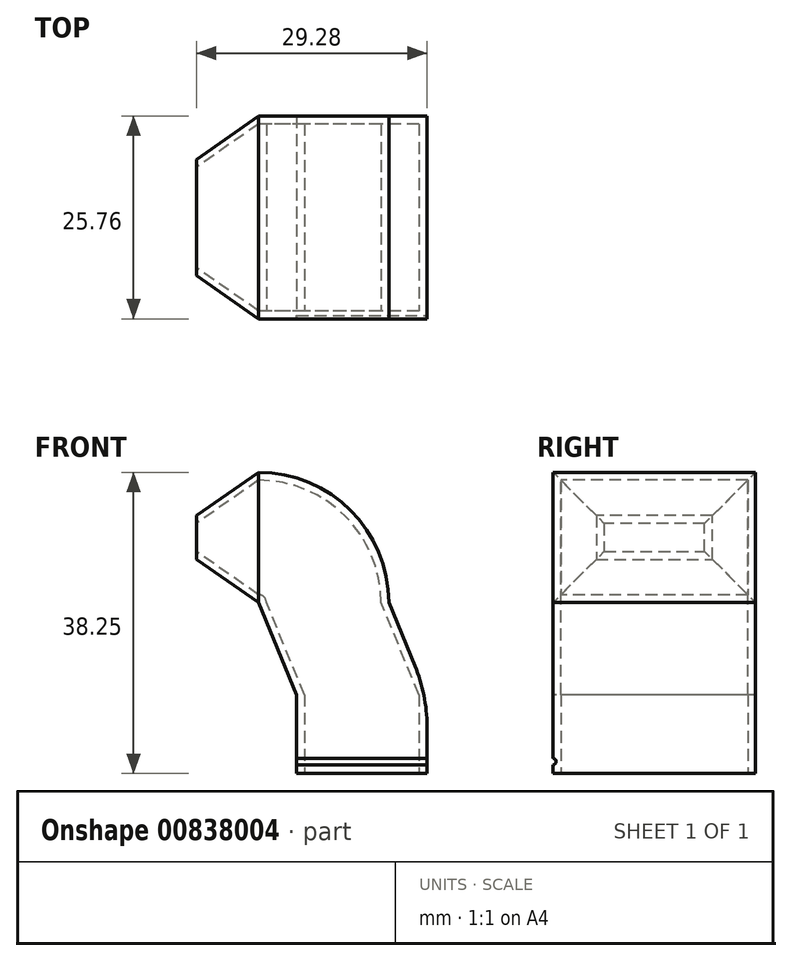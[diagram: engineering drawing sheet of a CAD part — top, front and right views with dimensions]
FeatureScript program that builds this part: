
annotation { "Feature Type Name" : "Feature", "Feature Type Description" : "" }
export const myFeature = defineFeature(function(context is Context, id is Id, definition is map)
    precondition{}
    {
        {
            var Q0;
            Q0=qCreatedBy(makeId("Top.planeOp"),FACE);
            var sketch = newSketch(context, id + "F0", { "sketchPlane" : qUnion([Q0])});
            skLineSegment(sketch, "E0.bottom", {"start": v(8.28, 12.88) * mm, "end": v(-8.27, 12.88) * mm});
            skLineSegment(sketch, "E0.top", {"start": v(8.28, -12.88) * mm, "end": v(-8.28, -12.88) * mm});
            skLineSegment(sketch, "E0.left", {"start": v(8.28, 12.88) * mm, "end": v(8.28, -12.88) * mm});
            skLineSegment(sketch, "E0.right", {"start": v(-8.27, 12.88) * mm, "end": v(-8.28, -12.88) * mm});
            skPoint(sketch, "E0.middle", {"position": v(0, 0) * mm});
            skLineSegment(sketch, "E1.0", {"start": v(-7.27, 11.88) * mm, "end": v(-7.28, -11.88) * mm});
            skLineSegment(sketch, "E1.1", {"start": v(7.28, 11.88) * mm, "end": v(-7.27, 11.88) * mm});
            skLineSegment(sketch, "E1.2", {"start": v(7.28, 11.88) * mm, "end": v(7.28, -11.88) * mm});
            skLineSegment(sketch, "E1.3", {"start": v(7.28, -11.88) * mm, "end": v(-7.28, -11.88) * mm});
            skSolve(sketch);
        }
        {
            var Q0;
            Q0=qSketchRegion(id+"F0",true);
            extrude(context, id + "F1", {"entities" : qUnion([Q0]), "depth" : 10 * mm, "offsetDistance" : 25 * mm});
        }
        {
            var Q0;
            Q0=makeQuery(id+"F1.opExtrude","SWEPT_FACE",FACE,{"disambiguationData":[OSD([sQuery(id+"F0.wireOp",EDGE,"E0.left")])]});
            var sketch = newSketch(context, id + "F2", { "sketchPlane" : qUnion([Q0])});
            skCircle(sketch, "E2", {"center": v(-12.88, 1.5) * mm, "radius": 0.4 * mm});
            skSolve(sketch);
        }
        {
            var Q0;
            {var subQ0=sQuery(id+"F2.wireOp",EDGE,"E2");var subQ1=makeQuery(id+"F1.opExtrude","SWEPT_EDGE",EDGE,{"disambiguationData":[OSD([sQuery(id+"F0.wireOp",EDGE,"E0.top"),sQuery(id+"F0.wireOp",EDGE,"E0.left")])]});var subQ2=makeQuery(id+"F2.imprint","INTERSECT",VERTEX,{"disambiguationData":[OD(0.0)],"derivedFrom":[subQ1,subQ0]});Q0=makeQuery(id+"F2.imprint","IMPRINT",FACE,{"disambiguationData":[TD([[makeQuery(id+"F2.imprint","IMPRINT",EDGE,{"disambiguationData":[TD([[subQ2,-1.0]])],"derivedFrom":subQ0}),1.0]])]});}
            extrude(context, id + "F3", {"entities" : qUnion([Q0]), "operationType" : NewBodyOperationType.REMOVE, "oppositeDirection" : true, "depth" : 25 * mm, "offsetDistance" : 25 * mm});
        }
        {
            var Q0;
            Q0=makeQuery(id+"F1.opExtrude","CAP_EDGE",EDGE,{"disambiguationData":[OSD([sQuery(id+"F0.wireOp",EDGE,"E0.right")])],"isStart":false});
            cPlane(context, id + "F4", {"entities" : qUnion([Q0]), "cplaneType" : CPlaneType.LINE_ANGLE, "offset" : 25 * mm, "angle" : 45 * degree, "width" : 150 * mm, "height" : 150 * mm});
        }
        {
            var Q0;
            Q0=qCreatedBy(id+"F4.planeOp",FACE);
            var sketch = newSketch(context, id + "F5", { "sketchPlane" : qUnion([Q0])});
            skLineSegment(sketch, "E3.0", {"start": v(1.22, -12.88) * mm, "end": v(1.22, 12.88) * mm});
            skLineSegment(sketch, "E4.bottom", {"start": v(1.22, 12.88) * mm, "end": v(17.77, 12.88) * mm});
            skLineSegment(sketch, "E4.top", {"start": v(1.22, -12.88) * mm, "end": v(17.77, -12.88) * mm});
            skLineSegment(sketch, "E4.left", {"start": v(1.22, 12.88) * mm, "end": v(1.22, -12.88) * mm});
            skLineSegment(sketch, "E4.right", {"start": v(17.77, 12.88) * mm, "end": v(17.77, -12.88) * mm});
            skLineSegment(sketch, "E5.0", {"start": v(16.77, 11.88) * mm, "end": v(16.77, -11.88) * mm});
            skLineSegment(sketch, "E5.1", {"start": v(2.22, 11.88) * mm, "end": v(16.77, 11.88) * mm});
            skLineSegment(sketch, "E5.2", {"start": v(2.22, 11.88) * mm, "end": v(2.22, -11.88) * mm});
            skLineSegment(sketch, "E5.3", {"start": v(2.22, -11.88) * mm, "end": v(16.77, -11.88) * mm});
            skSolve(sketch);
        }
        {
            var Q0;
            Q0=qCreatedBy(makeId("Front.planeOp"),FACE);
            var sketch = newSketch(context, id + "F6", { "sketchPlane" : qUnion([Q0])});
            skLineSegment(sketch, "E6", {"start": v(3.43, 21.7) * mm, "end": v(8.28, 10) * mm});
            skSolve(sketch);
        }
        {
            var Q0;
            Q0=makeQuery(id+"F1.opExtrude","CAP_FACE",FACE,{"disambiguationData":[OSD([sQuery(id+"F0.wireOp",EDGE,"E0.bottom"),sQuery(id+"F0.wireOp",EDGE,"E0.top"),sQuery(id+"F0.wireOp",EDGE,"E0.left"),sQuery(id+"F0.wireOp",EDGE,"E0.right"),sQuery(id+"F0.wireOp",EDGE,"E1.0"),sQuery(id+"F0.wireOp",EDGE,"E1.1"),sQuery(id+"F0.wireOp",EDGE,"E1.2"),sQuery(id+"F0.wireOp",EDGE,"E1.3")])],"isStart":false});
            var Q1;
            Q1=qConstructionFilter(qBodyType(qCreatedBy(id+"F6",EDGE),BodyType.WIRE),ConstructionObject.NO);
            sweep(context, id + "F7", {"operationType" : NewBodyOperationType.ADD, "profiles" : qUnion([Q0]), "path" : qUnion([Q1]), "keepProfileOrientation" : true});
        }
        {
            var Q0;
            {var subQ0=sQuery(id+"F0.wireOp",EDGE,"E0.left");Q0=makeQuery(id+"F7.boolean.opBoolean","MERGE",EDGE,{"derivedFrom":[makeQuery(id+"F1.opExtrude","CAP_EDGE",EDGE,{"disambiguationData":[OSD([subQ0])],"isStart":false}),makeQuery(id+"F7.opSweep","CAP_EDGE",EDGE,{"disambiguationData":[OSD([subQ0,sQuery(id+"F6.wireOp",VERTEX,"E6.end")])],"isStart":true})]});}
            fillet(context, id + "F8", {"entities" : qUnion([Q0]), "radius" : 20 * mm, "tangentPropagation" : true, "allowEdgeOverflow" : false});
        }
        {
            var Q0;
            Q0=qCreatedBy(makeId("Right.planeOp"),FACE);
            var Q1;
            Q1=makeQuery(id+"F7.opSweep","CAP_VERTEX",VERTEX,{"disambiguationData":[OSD([sQuery(id+"F0.wireOp",EDGE,"E0.bottom"),sQuery(id+"F0.wireOp",EDGE,"E0.right"),sQuery(id+"F6.wireOp",EDGE,"E6")])],"isStart":false});
            cPlane(context, id + "F9", {"entities" : qUnion([Q0, Q1]), "cplaneType" : CPlaneType.PLANE_POINT, "offset" : 13 * mm, "oppositeDirection" : true, "width" : 150 * mm, "height" : 150 * mm});
        }
        {
            var Q0;
            Q0=qCreatedBy(id+"F9.planeOp",FACE);
            var sketch = newSketch(context, id + "F10", { "sketchPlane" : qUnion([Q0])});
            skLineSegment(sketch, "E7.0", {"start": v(12.88, 21.7) * mm, "end": v(-12.88, 21.7) * mm});
            skLineSegment(sketch, "E8.top", {"start": v(12.88, 38.25) * mm, "end": v(-12.88, 38.25) * mm});
            skLineSegment(sketch, "E8.left", {"start": v(12.87, 21.7) * mm, "end": v(12.88, 38.25) * mm});
            skLineSegment(sketch, "E8.right", {"start": v(-12.88, 21.7) * mm, "end": v(-12.88, 38.25) * mm});
            skSolve(sketch);
        }
        {
            var Q0;
            Q0=qCreatedBy(makeId("Front.planeOp"),FACE);
            var sketch = newSketch(context, id + "F11", { "sketchPlane" : qUnion([Q0])});
            skLineSegment(sketch, "E9", {"start": v(3.43, 21.7) * mm, "end": v(3.43, 21.7) * mm});
            skLineSegment(sketch, "E10", {"start": v(-13.12, 38.25) * mm, "end": v(-13.12, 38.25) * mm});
            skPoint(sketch, "E11.visualSharp", {"position": v(3.43, 38.25) * mm});
            skArc(sketch, "E11.filletArc", {"start": v(3.43, 21.7) * mm, "mid": v(-1.42, 33.4) * mm, "end": v(-13.12, 38.25) * mm});
            skSolve(sketch);
        }
        {
            var Q0;
            Q0=makeQuery(id+"F7.opSweep","CAP_FACE",FACE,{"disambiguationData":[OSD([sQuery(id+"F0.wireOp",EDGE,"E0.bottom"),sQuery(id+"F0.wireOp",EDGE,"E0.top"),sQuery(id+"F0.wireOp",EDGE,"E0.left"),sQuery(id+"F0.wireOp",EDGE,"E0.right"),sQuery(id+"F0.wireOp",EDGE,"E1.0"),sQuery(id+"F0.wireOp",EDGE,"E1.1"),sQuery(id+"F0.wireOp",EDGE,"E1.2"),sQuery(id+"F0.wireOp",EDGE,"E1.3"),sQuery(id+"F6.wireOp",VERTEX,"E6.start")])],"isStart":false});
            var Q1;
            Q1=sQuery(id+"F11.wireOp",EDGE,"E11.filletArc");
            sweep(context, id + "F12", {"operationType" : NewBodyOperationType.ADD, "profiles" : qUnion([Q0]), "path" : qUnion([Q1])});
        }
        {
            var Q0;
            Q0=qCreatedBy(makeId("Right.planeOp"),FACE);
            cPlane(context, id + "F13", {"entities" : qUnion([Q0]), "cplaneType" : CPlaneType.OFFSET, "offset" : 21 * mm, "oppositeDirection" : true, "width" : 150 * mm, "height" : 150 * mm});
        }
        {
            var Q0;
            Q0=qCreatedBy(id+"F13.planeOp",FACE);
            var sketch = newSketch(context, id + "F14", { "sketchPlane" : qUnion([Q0])});
            skLineSegment(sketch, "E12.0", {"start": v(7.38, 32.75) * mm, "end": v(-7.38, 32.75) * mm});
            skLineSegment(sketch, "E12.1", {"start": v(7.38, 27.2) * mm, "end": v(7.38, 32.75) * mm});
            skLineSegment(sketch, "E12.2", {"start": v(-7.38, 27.2) * mm, "end": v(7.38, 27.2) * mm});
            skLineSegment(sketch, "E12.3", {"start": v(-7.38, 32.75) * mm, "end": v(-7.38, 27.2) * mm});
            skLineSegment(sketch, "E13.0", {"start": v(6.38, 31.75) * mm, "end": v(-6.38, 31.75) * mm});
            skLineSegment(sketch, "E13.1", {"start": v(6.38, 28.2) * mm, "end": v(6.38, 31.75) * mm});
            skLineSegment(sketch, "E13.2", {"start": v(-6.38, 28.2) * mm, "end": v(6.38, 28.2) * mm});
            skLineSegment(sketch, "E13.3", {"start": v(-6.38, 31.75) * mm, "end": v(-6.38, 28.2) * mm});
            skSolve(sketch);
        }
        {
            var Q0;
            Q0=qCreatedBy(makeId("Front.planeOp"),FACE);
            var sketch = newSketch(context, id + "F15", { "sketchPlane" : qUnion([Q0])});
            skLineSegment(sketch, "E14.0", {"start": v(-13.12, 21.7) * mm, "end": v(-13.12, 38.25) * mm});
            skLineSegment(sketch, "E15.0", {"start": v(-21, 27.2) * mm, "end": v(-21, 32.75) * mm});
            skLineSegment(sketch, "E16", {"start": v(-21, 32.75) * mm, "end": v(-13.12, 38.25) * mm});
            skLineSegment(sketch, "E17", {"start": v(-21, 27.2) * mm, "end": v(-13.12, 21.7) * mm});
            skLineSegment(sketch, "E18.0", {"start": v(-21, 28.2) * mm, "end": v(-21, 31.75) * mm});
            skLineSegment(sketch, "E19.0", {"start": v(-13.12, 22.7) * mm, "end": v(-13.12, 37.25) * mm});
            skLineSegment(sketch, "E20", {"start": v(-13.12, 37.25) * mm, "end": v(-21, 31.75) * mm});
            skSolve(sketch);
        }
        {
            var Q0;
            {var subQ0=sQuery(id+"F15.wireOp",EDGE,"E16");Q0=makeQuery(id+"F15.imprint","IMPRINT",FACE,{"disambiguationData":[TD([[makeQuery(id+"F15.imprint","IMPRINT",EDGE,{"derivedFrom":subQ0}),-1.0]])]});}
            var Q1;
            Q1=sQuery(id+"F14.wireOp",EDGE,"E12.3");
            var Q2;
            Q2=sQuery(id+"F14.wireOp",EDGE,"E12.0");
            var Q3;
            Q3=sQuery(id+"F14.wireOp",EDGE,"E12.1");
            var Q4;
            Q4=sQuery(id+"F14.wireOp",EDGE,"E12.2");
            sweep(context, id + "F16", {"operationType" : NewBodyOperationType.ADD, "profiles" : qUnion([Q0]), "path" : qUnion([Q1, Q2, Q3, Q4])});
        }
    });
